# Revit family: Shower-Trim_and_Valve-KOHLER-MODULO-K-97365T
name_source: partatom
category: Plumbing Fixtures
revit_build: Autodesk Revit 2017 (Build: 20160225_1515(x64)
units: mm (PartAtom-declared; Revit-internal decimal feet)

## family parameters
Cut with Voids When Loaded = No
Host = Face
OmniClass Number = 23.31.25.00
OmniClass Title = Toilet and Bath Specialties
Part Type = Normal
Room Calculation Point = No
Round Connector Dimension = Use Diameter
Shared = No

## types (2) — shared parameters
ADA Compliant = No
Assembly Code = D2010
CW Connection = Yes
Cold Water Inlet = Cold Water Inlet
Date Modified = 06/03/2020
Description = RECESSED S/O TRIM AND VALVE-AVID
Drain Included = No
Flow Rate = 0 GPM
HW Connection = Yes
Height = 7 1/8"
Hot Water Inlet = Hot Water Inlet
Length = 3 7/16"
Manufacturer = KOHLER Co.
Master Format 2014 = 22 41 39
Master Format 2014 Name = Residential Faucets, Supplies, and Trim
Material = Premium Metal Construction
Pressure = 0.00 psi
Product Name = MODULO
Tempered Water Outlet = Tempered Water Outlet
URL = http://www.kohler.com.cn
Vent Connection = No
Waste Connection = No
Waste Water Outlet = Waste Water Outlet
WaterSense Certified = No
Width = 7 1/8"

## per-type parameters (varying)
| type | Default Elevation | Finish | Model | Type |
| CP-Polished Chrome | 42" | Kohler-Metal-CP-Polished_Chrome | K-97365T-4-CP | 1 |
| TT-Silver Titanium | 36" | Kohler-Metal-TT-Titanium_Silver | K-97365T-4-TT | 2 |

## geometry (parser evidence)
native form markers: Sweep x4
no freeform markers — native parametric forms only
